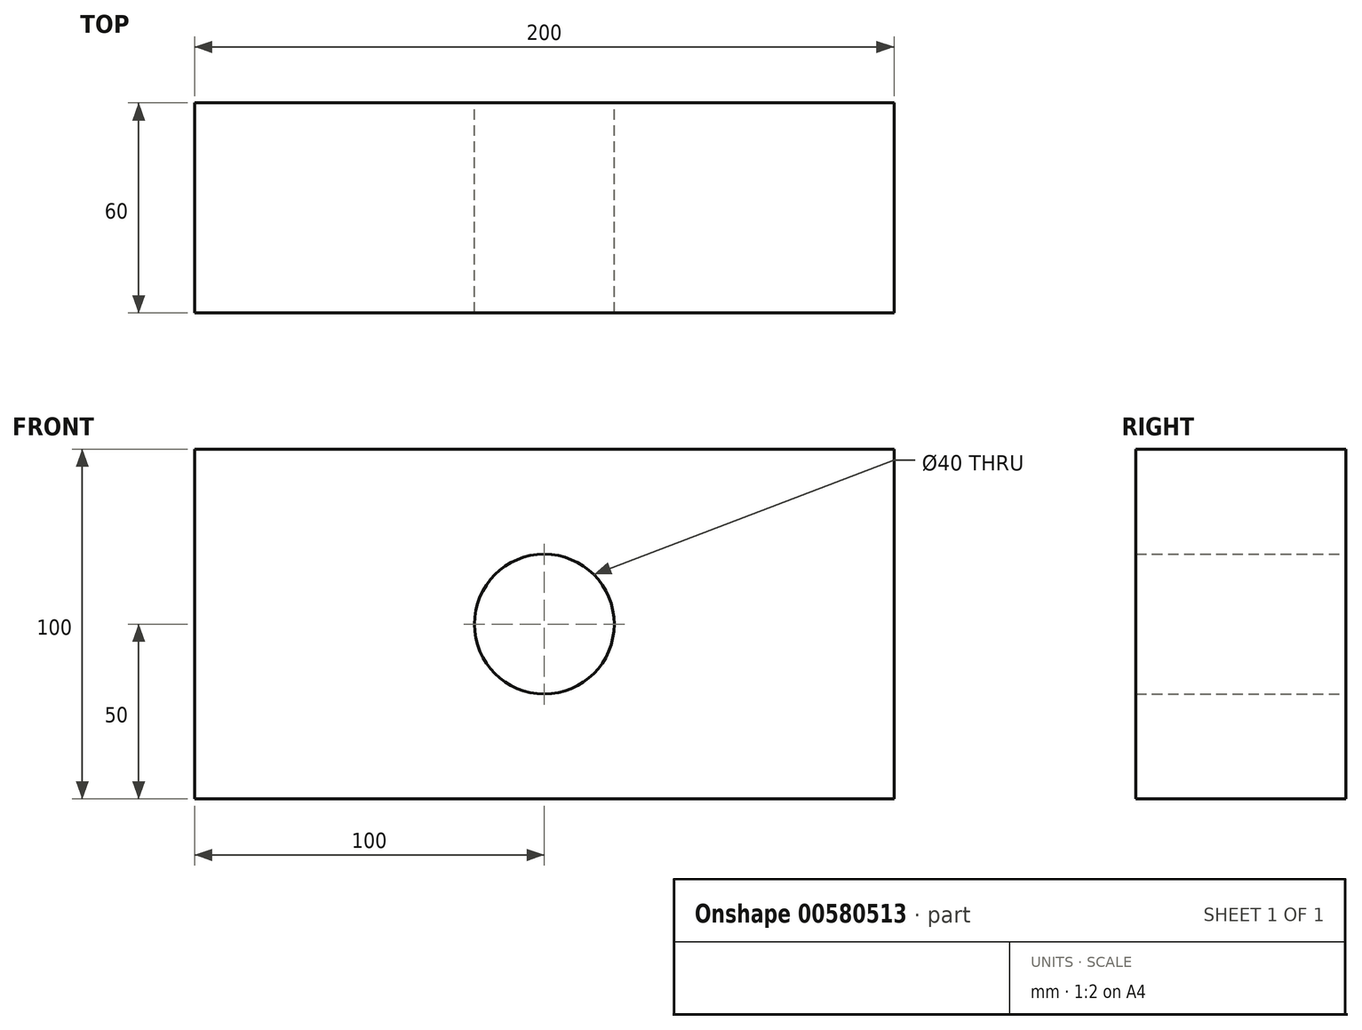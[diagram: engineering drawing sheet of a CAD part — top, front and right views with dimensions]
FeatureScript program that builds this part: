
annotation { "Feature Type Name" : "Feature", "Feature Type Description" : "" }
export const myFeature = defineFeature(function(context is Context, id is Id, definition is map)
    precondition{}
    {
        {
            var Q0;
            Q0=qCreatedBy(makeId("Front.planeOp"),FACE);
            var sketch = newSketch(context, id + "F0", { "sketchPlane" : qUnion([Q0])});
            skLineSegment(sketch, "E0.bottom", {"start": v(100, 50) * mm, "end": v(-100, 50) * mm});
            skLineSegment(sketch, "E0.top", {"start": v(100, -50) * mm, "end": v(-100, -50) * mm});
            skLineSegment(sketch, "E0.left", {"start": v(100, 50) * mm, "end": v(100, -50) * mm});
            skLineSegment(sketch, "E0.right", {"start": v(-100, 50) * mm, "end": v(-100, -50) * mm});
            skPoint(sketch, "E0.middle", {"position": v(0, 0) * mm});
            skSolve(sketch);
        }
        {
            var Q0;
            Q0 = qSketchRegion(id + "F0", true);
            extrude(context, id + "F1", {"entities" : qUnion([Q0]), "depth" : 60 * mm, "offsetDistance" : 25 * mm, "symmetric" : true});
        }
        {
            var Q0;
            Q0=makeQuery(id+"F1.opExtrude","CAP_FACE",FACE,{"disambiguationData":[OSD([sQuery(id+"F0.wireOp",EDGE,"E0.bottom"),sQuery(id+"F0.wireOp",EDGE,"E0.top"),sQuery(id+"F0.wireOp",EDGE,"E0.left"),sQuery(id+"F0.wireOp",EDGE,"E0.right")])],"isStart":false});
            var sketch = newSketch(context, id + "F2", { "sketchPlane" : qUnion([Q0])});
            skCircle(sketch, "E1", {"center": v(0, 0) * mm, "radius": 20 * mm});
            skSolve(sketch);
        }
        {
            var Q0;
            Q0 = qSketchRegion(id + "F2", true);
            extrude(context, id + "F3", {"entities" : qUnion([Q0]), "operationType" : NewBodyOperationType.REMOVE, "depth" : 120 * mm, "offsetDistance" : 25 * mm, "symmetric" : true});
        }
    });
